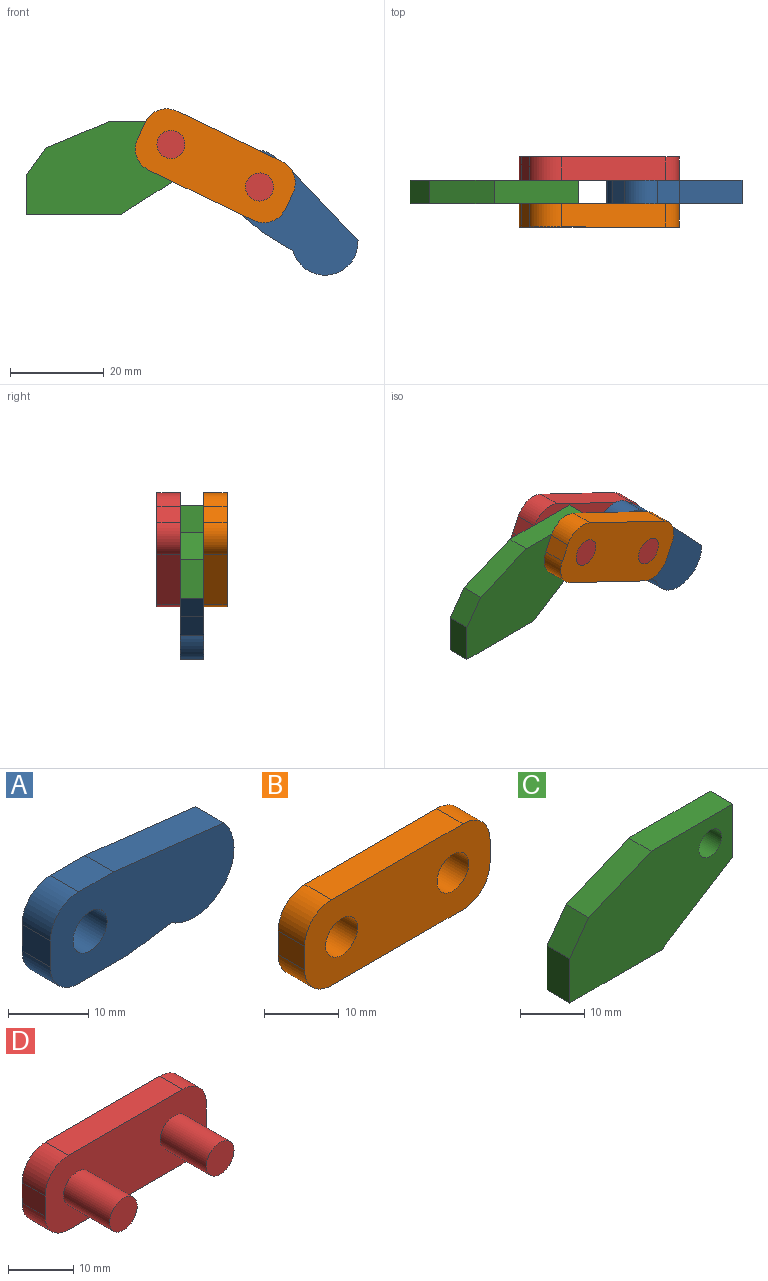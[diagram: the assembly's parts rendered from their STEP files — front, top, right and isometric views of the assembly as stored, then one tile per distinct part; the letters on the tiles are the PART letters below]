
ASSEMBLY  parts=4 mates=3
PART A: 11 faces, bbox 32.4x5x14.1 mm
  f0: cylinder r=7.07mm len=11.83mm, axis (0,1,0), area 102.9mm2, adj f1,f5,f7,f8
  f1: plane 19.43x5mm, normal (0.11,0,0.99), area 97.8mm2, adj f0,f2,f7,f8
  f2: plane 6.1x5mm, normal (0,0,1), area 30.5mm2, adj f1,f7,f8,f10
  f3: plane 5x4mm, normal (-1,0,0), area 20mm2, adj f7,f8,f9,f10
  f4: plane 8.67x5mm, normal (0,0,-1), area 43.3mm2, adj f5,f7,f8,f9
  f5: plane 7.64x5mm, normal (0.15,0,-0.99), area 38.7mm2, adj f0,f4,f7,f8
  f6: cylinder r=3mm len=6mm, axis (0,1,0), area 94.2mm2, adj f7,f8
  f7: plane 32.37x14.07mm, normal (0,-1,0), area 369.6mm2, adj f0,f1,f2,f3,f4,f5,f6,f9
  f8: plane 32.37x14.07mm, normal (0,1,0), area 369.6mm2, adj f0,f1,f2,f3,f4,f5,f6,f9
  f9: cylinder r=5mm len=5mm, axis (0,-1,0), area 39.3mm2, adj f3,f4,f7,f8
  f10: cylinder r=5mm len=5mm, axis (0,1,0), area 39.3mm2, adj f2,f3,f7,f8
PART B: 12 faces, bbox 35x5x14 mm
  f0: plane 5x3.84mm, normal (-1,0,0), area 19.2mm2, adj f6,f7,f8,f11
  f1: plane 24.84x5mm, normal (0,0,-1), area 124.2mm2, adj f6,f7,f8,f9
  f2: plane 5x3.84mm, normal (1,0,0), area 19.2mm2, adj f6,f7,f9,f10
  f3: cylinder r=3mm len=6mm, axis (0,1,0), area 94.2mm2, adj f6,f7
  f4: cylinder r=3mm len=6mm, axis (0,1,0), area 94.2mm2, adj f6,f7
  f5: plane 24.84x5mm, normal (0,0,1), area 124.2mm2, adj f6,f7,f10,f11
  f6: plane 35x14mm, normal (0,-1,0), area 411.3mm2, adj f0,f1,f2,f3,f4,f5,f8,f9
  f7: plane 35x14mm, normal (0,1,0), area 411.3mm2, adj f0,f1,f2,f3,f4,f5,f8,f9
  f8: cylinder r=5.08mm len=5.08mm, axis (0,-1,0), area 39.9mm2, adj f0,f1,f6,f7
  f9: cylinder r=5.08mm len=5.08mm, axis (0,1,0), area 39.9mm2, adj f1,f2,f6,f7
  f10: cylinder r=5.08mm len=5.08mm, axis (0,-1,0), area 39.9mm2, adj f2,f5,f6,f7
  f11: cylinder r=5.08mm len=5.08mm, axis (0,1,0), area 39.9mm2, adj f0,f5,f6,f7
PART C: 10 faces, bbox 36x5x20 mm
  f0: plane 8.42x5mm, normal (-1,0,0), area 42.1mm2, adj f1,f3,f4,f5
  f1: plane 20.24x5mm, normal (0,0,-1), area 101.2mm2, adj f0,f4,f5,f6
  f2: plane 13.82x5.79mm, normal (-0.39,0,0.92), area 74.9mm2, adj f3,f4,f5,f8
  f3: plane 5.79x5mm, normal (-0.81,0,0.59), area 35.7mm2, adj f0,f2,f4,f5
  f4: plane 36x20mm, normal (0,-1,0), area 545.2mm2, adj f0,f1,f2,f3,f6,f7,f8,f9
  f5: plane 36x20mm, normal (0,1,0), area 545.2mm2, adj f0,f1,f2,f3,f6,f7,f8,f9
  f6: plane 15.76x10mm, normal (0.54,0,-0.84), area 93.3mm2, adj f1,f4,f5,f7
  f7: plane 10x5mm, normal (1,0,0), area 50mm2, adj f4,f5,f6,f8
  f8: plane 18x5mm, normal (0,0,1), area 90mm2, adj f2,f4,f5,f7
  f9: cylinder r=2.5mm len=5mm, axis (0,1,0), area 78.5mm2, adj f4,f5
PART D: 18 faces, bbox 35x15x14 mm
  f0: cylinder r=3mm len=6mm, axis (0,1,0), area 2.8mm2, adj f7,f15
  f1: cylinder r=3mm len=6mm, axis (0,1,0), area 2.8mm2, adj f7,f12
  f2: plane 5x3.84mm, normal (-1,0,0), area 19.2mm2, adj f6,f7,f8,f11
  f3: plane 24.84x5mm, normal (0,0,-1), area 124.2mm2, adj f6,f7,f8,f9
  f4: plane 5x3.84mm, normal (1,0,0), area 19.2mm2, adj f6,f7,f9,f10
  f5: plane 24.84x5mm, normal (0,0,1), area 124.2mm2, adj f6,f7,f10,f11
  f6: plane 35x14mm, normal (0,-1,0), area 411.3mm2, adj f2,f3,f4,f5,f8,f9,f10,f11
  f7: plane 35x14mm, normal (0,1,0), area 411.3mm2, adj f0,f1,f2,f3,f4,f5,f8,f9
  f8: cylinder r=5.08mm len=5.08mm, axis (0,-1,0), area 39.9mm2, adj f2,f3,f6,f7
  f9: cylinder r=5.08mm len=5.08mm, axis (0,1,0), area 39.9mm2, adj f3,f4,f6,f7
  f10: cylinder r=5.08mm len=5.08mm, axis (0,-1,0), area 39.9mm2, adj f4,f5,f6,f7
  f11: cylinder r=5.08mm len=5.08mm, axis (0,1,0), area 39.9mm2, adj f2,f5,f6,f7
  f12: plane 6x6mm, normal (0,1,0), area 28.3mm2, adj f1
  f13: cylinder r=3mm len=10mm, axis (0,1,0), area 188.5mm2, adj f6,f14
  f14: plane 6x6mm, normal (0,-1,0), area 28.3mm2, adj f13
  f15: plane 6x6mm, normal (0,1,0), area 28.3mm2, adj f0
  f16: cylinder r=3mm len=10mm, axis (0,1,0), area 188.5mm2, adj f6,f17
  f17: plane 6x6mm, normal (0,-1,0), area 28.3mm2, adj f16
PLACE A rot(axis=(0,1,0),40.1deg) t=(7.93,-13.86,12.12)mm
PLACE B rot(axis=(0,1,0),25.6deg) t=(-10.48,-18.86,18.76)mm
PLACE C t=(-32.14,-13.86,7.04)mm fixed
PLACE D rot(axis=(0,1,0),25.6deg) t=(-10.48,-8.86,18.76)mm
MATE fastened B.f3 <-> D.f0  axis (0,-1,0) through (-1.14,-23.86,22.04)mm
MATE revolute D.f0 <-> C.f9  axis (0,1,0) through (-1.14,-18.86,22.04)mm
MATE revolute A.f6 <-> D.f1  axis (0,1,0) through (17.79,-13.86,12.96)mm
